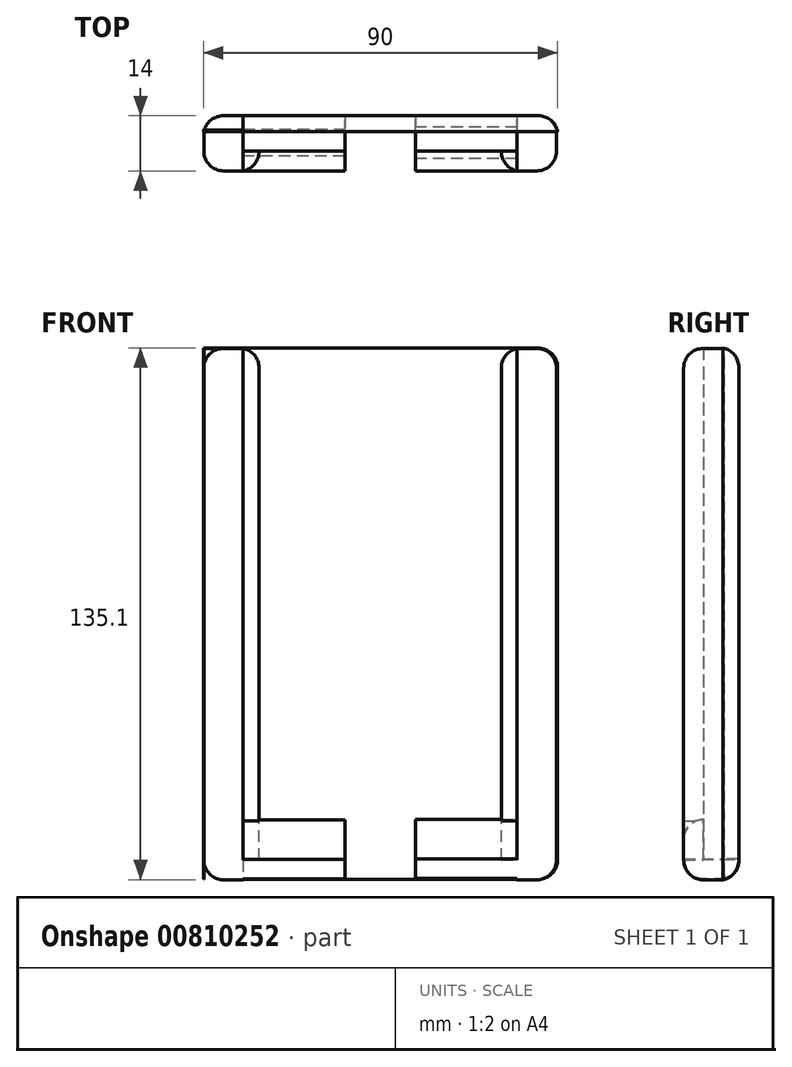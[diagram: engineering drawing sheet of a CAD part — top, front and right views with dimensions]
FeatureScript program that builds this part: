
annotation { "Feature Type Name" : "Feature", "Feature Type Description" : "" }
export const myFeature = defineFeature(function(context is Context, id is Id, definition is map)
    precondition{}
    {
        {
            var Q0;
            Q0=qCreatedBy(makeId("Front.planeOp"),FACE);
            var sketch = newSketch(context, id + "F0", { "sketchPlane" : qUnion([Q0])});
            skLineSegment(sketch, "E0.bottom", {"start": v(45, -67.5) * mm, "end": v(-45, -67.5) * mm});
            skLineSegment(sketch, "E0.top", {"start": v(45, 67.5) * mm, "end": v(-45, 67.5) * mm});
            skLineSegment(sketch, "E0.left", {"start": v(45, -67.5) * mm, "end": v(45, 67.5) * mm});
            skLineSegment(sketch, "E0.right", {"start": v(-45, -67.5) * mm, "end": v(-45, 67.5) * mm});
            skPoint(sketch, "E0.middle", {"position": v(0, 0) * mm});
            skSolve(sketch);
        }
        {
            var Q0;
            Q0=makeQuery(id+"F0.imprint","IMPRINT",FACE,{"disambiguationData":[TD([[makeQuery(id+"F0.imprint","IMPRINT",EDGE,{"derivedFrom":sQuery(id+"F0.wireOp",EDGE,"E0.bottom")}),-1.0]])]});
            var sketch = newSketch(context, id + "F1", { "sketchPlane" : qUnion([Q0])});
            skLineSegment(sketch, "E1.bottom", {"start": v(-44.9, -67.6) * mm, "end": v(-34.9, -67.6) * mm});
            skLineSegment(sketch, "E1.top", {"start": v(-44.9, 67.4) * mm, "end": v(-34.9, 67.4) * mm});
            skLineSegment(sketch, "E1.left", {"start": v(-44.9, -67.6) * mm, "end": v(-44.9, 67.4) * mm});
            skLineSegment(sketch, "E1.right", {"start": v(-34.9, -67.6) * mm, "end": v(-34.9, 67.4) * mm});
            skSolve(sketch);
        }
        {
            var Q0;
            Q0=makeQuery(id+"F0.imprint","IMPRINT",FACE,{"disambiguationData":[TD([[makeQuery(id+"F0.imprint","IMPRINT",EDGE,{"derivedFrom":sQuery(id+"F0.wireOp",EDGE,"E0.bottom")}),-1.0]])]});
            var sketch = newSketch(context, id + "F2", { "sketchPlane" : qUnion([Q0])});
            skLineSegment(sketch, "E2.bottom", {"start": v(44.68, -67.6) * mm, "end": v(34.68, -67.6) * mm});
            skLineSegment(sketch, "E2.top", {"start": v(44.68, 67.4) * mm, "end": v(34.68, 67.4) * mm});
            skLineSegment(sketch, "E2.left", {"start": v(44.68, -67.6) * mm, "end": v(44.68, 67.4) * mm});
            skLineSegment(sketch, "E2.right", {"start": v(34.68, -67.6) * mm, "end": v(34.68, 67.4) * mm});
            skSolve(sketch);
        }
        {
            var Q0;
            Q0=qCreatedBy(makeId("Front.planeOp"),FACE);
            var sketch = newSketch(context, id + "F3", { "sketchPlane" : qUnion([Q0])});
            skLineSegment(sketch, "E3.bottom", {"start": v(34.83, -67.26) * mm, "end": v(8.83, -67.26) * mm});
            skLineSegment(sketch, "E3.top", {"start": v(34.83, -62.26) * mm, "end": v(8.83, -62.26) * mm});
            skLineSegment(sketch, "E3.left", {"start": v(34.83, -67.26) * mm, "end": v(34.83, -62.26) * mm});
            skLineSegment(sketch, "E3.right", {"start": v(8.83, -67.26) * mm, "end": v(8.83, -62.26) * mm});
            skSolve(sketch);
        }
        {
            var Q0;
            Q0=qCreatedBy(makeId("Front.planeOp"),FACE);
            var sketch = newSketch(context, id + "F4", { "sketchPlane" : qUnion([Q0])});
            skLineSegment(sketch, "E4.bottom", {"start": v(-35.09, -67.43) * mm, "end": v(-9.09, -67.43) * mm});
            skLineSegment(sketch, "E4.top", {"start": v(-35.09, -62.43) * mm, "end": v(-9.09, -62.43) * mm});
            skLineSegment(sketch, "E4.left", {"start": v(-35.09, -67.43) * mm, "end": v(-35.09, -62.43) * mm});
            skLineSegment(sketch, "E4.right", {"start": v(-9.09, -67.43) * mm, "end": v(-9.09, -62.43) * mm});
            skSolve(sketch);
        }
        {
            var Q0;
            Q0=qSketchRegion(id+"F1",true);
            extrude(context, id + "F5", {"entities" : qUnion([Q0]), "depth" : 4 * mm, "offsetDistance" : 25 * mm});
        }
        {
            var Q0;
            Q0=qSketchRegion(id+"F2",true);
            extrude(context, id + "F6", {"entities" : qUnion([Q0]), "depth" : 4 * mm, "offsetDistance" : 25 * mm});
        }
        {
            var Q0;
            Q0=qSketchRegion(id+"F3",true);
            extrude(context, id + "F7", {"entities" : qUnion([Q0]), "operationType" : NewBodyOperationType.ADD, "depth" : 4 * mm, "offsetDistance" : 25 * mm});
        }
        {
            var Q0;
            Q0=qSketchRegion(id+"F4",true);
            extrude(context, id + "F8", {"entities" : qUnion([Q0]), "operationType" : NewBodyOperationType.ADD, "depth" : 4 * mm, "offsetDistance" : 25 * mm});
        }
        {
            var Q0;
            {var subQ1=sQuery(id+"F1.wireOp",EDGE,"E1.top");Q0=makeQuery(id+"F1.imprint","IMPRINT",FACE,{"disambiguationData":[TD([[makeQuery(id+"F1.imprint","IMPRINT",EDGE,{"derivedFrom":subQ1}),1.0]])]});}
            extrude(context, id + "F9", {"entities" : qUnion([Q0]), "depth" : 4 * mm, "offsetDistance" : 25 * mm});
        }
        {
            var Q0;
            Q0=makeQuery(id+"F8.boolean.opBoolean","MERGE",FACE,{"derivedFrom":[makeQuery(id+"F5.opExtrude","CAP_FACE",FACE,{"disambiguationData":[OSD([sQuery(id+"F1.wireOp",EDGE,"E1.bottom"),sQuery(id+"F1.wireOp",EDGE,"E1.top"),sQuery(id+"F1.wireOp",EDGE,"E1.left"),sQuery(id+"F1.wireOp",EDGE,"E1.right")])],"isStart":false}),makeQuery(id+"F8.opExtrude","CAP_FACE",FACE,{"disambiguationData":[OSD([sQuery(id+"F4.wireOp",EDGE,"E4.bottom"),sQuery(id+"F4.wireOp",EDGE,"E4.top"),sQuery(id+"F4.wireOp",EDGE,"E4.left"),sQuery(id+"F4.wireOp",EDGE,"E4.right")])],"isStart":false})]});
            var Q1;
            Q1=makeQuery(id+"F7.boolean.opBoolean","MERGE",FACE,{"derivedFrom":[makeQuery(id+"F6.opExtrude","CAP_FACE",FACE,{"disambiguationData":[OSD([sQuery(id+"F2.wireOp",EDGE,"E2.bottom"),sQuery(id+"F2.wireOp",EDGE,"E2.top"),sQuery(id+"F2.wireOp",EDGE,"E2.left"),sQuery(id+"F2.wireOp",EDGE,"E2.right")])],"isStart":false}),makeQuery(id+"F7.opExtrude","CAP_FACE",FACE,{"disambiguationData":[OSD([sQuery(id+"F3.wireOp",EDGE,"E3.bottom"),sQuery(id+"F3.wireOp",EDGE,"E3.top"),sQuery(id+"F3.wireOp",EDGE,"E3.left"),sQuery(id+"F3.wireOp",EDGE,"E3.right")])],"isStart":false})]});
            extrude(context, id + "F10", {"entities" : qUnion([Q0, Q1]), "depth" : 10 * mm, "offsetDistance" : 25 * mm});
        }
        {
            var Q0;
            Q0=makeQuery(id+"F10.opExtrude","SWEPT_FACE",FACE,{"disambiguationData":[OSD([sQuery(id+"F3.wireOp",EDGE,"E3.top")])]});
            var sketch = newSketch(context, id + "F11", { "sketchPlane" : qUnion([Q0])});
            skLineSegment(sketch, "E5.bottom", {"start": v(8.83, -14) * mm, "end": v(34.68, -14) * mm});
            skLineSegment(sketch, "E5.top", {"start": v(8.83, -9) * mm, "end": v(34.68, -9) * mm});
            skLineSegment(sketch, "E5.left", {"start": v(8.83, -14) * mm, "end": v(8.83, -9) * mm});
            skLineSegment(sketch, "E5.right", {"start": v(34.68, -14) * mm, "end": v(34.68, -9) * mm});
            skSolve(sketch);
        }
        {
            var Q0;
            Q0=makeQuery(id+"F10.opExtrude","SWEPT_FACE",FACE,{"disambiguationData":[OSD([sQuery(id+"F4.wireOp",EDGE,"E4.top")])]});
            var sketch = newSketch(context, id + "F12", { "sketchPlane" : qUnion([Q0])});
            skLineSegment(sketch, "E6.bottom", {"start": v(-34.9, -14) * mm, "end": v(-9.09, -14) * mm});
            skLineSegment(sketch, "E6.top", {"start": v(-34.9, -9) * mm, "end": v(-9.09, -9) * mm});
            skLineSegment(sketch, "E6.left", {"start": v(-34.9, -14) * mm, "end": v(-34.9, -9) * mm});
            skLineSegment(sketch, "E6.right", {"start": v(-9.09, -14) * mm, "end": v(-9.09, -9) * mm});
            skSolve(sketch);
        }
        {
            var Q0;
            Q0=makeQuery(id+"F12.imprint","IMPRINT",FACE,{"disambiguationData":[TD([[makeQuery(id+"F12.imprint","IMPRINT",EDGE,{"derivedFrom":sQuery(id+"F12.wireOp",EDGE,"E6.bottom")}),1.0]])]});
            var Q1;
            Q1=makeQuery(id+"F11.imprint","IMPRINT",FACE,{"disambiguationData":[TD([[makeQuery(id+"F11.imprint","IMPRINT",EDGE,{"derivedFrom":sQuery(id+"F11.wireOp",EDGE,"E5.bottom")}),-1.0]])]});
            extrude(context, id + "F13", {"entities" : qUnion([Q0, Q1]), "depth" : 10 * mm, "offsetDistance" : 25 * mm});
        }
        {
            var Q0;
            {var subQ0=sQuery(id+"F2.wireOp",EDGE,"E2.right");var subQ2=sQuery(id+"F2.wireOp",EDGE,"E2.top");Q0=makeQuery(id+"F10.opExtrude","SWEPT_FACE",FACE,{"disambiguationData":[OSD([subQ0]),TDD([makeQuery(id+"F7.boolean.opBoolean","SPLIT",EDGE,{"disambiguationData":[TD([makeQuery(id+"F6.opExtrude","SWEPT_FACE",FACE,{"disambiguationData":[OSD([subQ2])]})])],"derivedFrom":makeQuery(id+"F6.opExtrude","CAP_EDGE",EDGE,{"disambiguationData":[OSD([subQ0])],"isStart":false})})])]});}
            var sketch = newSketch(context, id + "F14", { "sketchPlane" : qUnion([Q0])});
            skLineSegment(sketch, "E7.bottom", {"start": v(14, 67.4) * mm, "end": v(9, 67.4) * mm});
            skLineSegment(sketch, "E7.top", {"start": v(14, -52.6) * mm, "end": v(9, -52.6) * mm});
            skLineSegment(sketch, "E7.left", {"start": v(14, 67.4) * mm, "end": v(14, -52.6) * mm});
            skLineSegment(sketch, "E7.right", {"start": v(9, 67.4) * mm, "end": v(9, -52.6) * mm});
            skSolve(sketch);
        }
        {
            var Q0;
            Q0=makeQuery(id+"F14.imprint","IMPRINT",FACE,{"disambiguationData":[TD([[makeQuery(id+"F14.imprint","IMPRINT",EDGE,{"derivedFrom":sQuery(id+"F14.wireOp",EDGE,"E7.bottom")}),1.0]])]});
            extrude(context, id + "F15", {"entities" : qUnion([Q0]), "depth" : 4 * mm, "offsetDistance" : 25 * mm});
        }
        {
            var Q0;
            {var subQ1=sQuery(id+"F1.wireOp",EDGE,"E1.right");var subQ2=sQuery(id+"F1.wireOp",EDGE,"E1.top");Q0=makeQuery(id+"F10.opExtrude","SWEPT_FACE",FACE,{"disambiguationData":[OSD([subQ1]),TDD([makeQuery(id+"F8.boolean.opBoolean","SPLIT",EDGE,{"disambiguationData":[TD([makeQuery(id+"F5.opExtrude","SWEPT_FACE",FACE,{"disambiguationData":[OSD([subQ2])]})])],"derivedFrom":makeQuery(id+"F5.opExtrude","CAP_EDGE",EDGE,{"disambiguationData":[OSD([subQ1])],"isStart":false})})])]});}
            var sketch = newSketch(context, id + "F16", { "sketchPlane" : qUnion([Q0])});
            skLineSegment(sketch, "E8.bottom", {"start": v(-14, 67.4) * mm, "end": v(-9, 67.4) * mm});
            skLineSegment(sketch, "E8.top", {"start": v(-14, -52.6) * mm, "end": v(-9, -52.6) * mm});
            skLineSegment(sketch, "E8.left", {"start": v(-14, 67.4) * mm, "end": v(-14, -52.6) * mm});
            skLineSegment(sketch, "E8.right", {"start": v(-9, 67.4) * mm, "end": v(-9, -52.6) * mm});
            skSolve(sketch);
        }
        {
            var Q0;
            Q0=makeQuery(id+"F16.imprint","IMPRINT",FACE,{"disambiguationData":[TD([[makeQuery(id+"F16.imprint","IMPRINT",EDGE,{"derivedFrom":sQuery(id+"F16.wireOp",EDGE,"E8.bottom")}),-1.0]])]});
            extrude(context, id + "F17", {"entities" : qUnion([Q0]), "depth" : 4 * mm, "offsetDistance" : 25 * mm});
        }
        {
            var Q0;
            Q0=makeQuery(id+"F10.opExtrude","SWEPT_EDGE",EDGE,{"disambiguationData":[OSD([sQuery(id+"F1.wireOp",EDGE,"E1.bottom"),sQuery(id+"F1.wireOp",EDGE,"E1.left")])]});
            var Q1;
            Q1=makeQuery(id+"F9.opExtrude","SWEPT_EDGE",EDGE,{"disambiguationData":[OSD([sQuery(id+"F0.wireOp",EDGE,"E0.bottom"),sQuery(id+"F0.wireOp",EDGE,"E0.right")])]});
            fillet(context, id + "F18", {"entities" : qUnion([Q0, Q1]), "radius" : 5 * mm, "tangentPropagation" : true, "allowEdgeOverflow" : false});
        }
        {
            var Q0;
            Q0=makeQuery(id+"F5.opExtrude","SWEPT_EDGE",EDGE,{"disambiguationData":[OSD([sQuery(id+"F1.wireOp",EDGE,"E1.bottom"),sQuery(id+"F1.wireOp",EDGE,"E1.left")])]});
            var Q1;
            {var subQ0=sQuery(id+"F0.wireOp",EDGE,"E0.right");Q1=makeQuery(id+"F18.opFillet","BLEND_EDGE",EDGE,{"blendedFrom":[makeQuery(id+"F9.opExtrude","SWEPT_EDGE",EDGE,{"disambiguationData":[OSD([sQuery(id+"F0.wireOp",EDGE,"E0.bottom"),subQ0])]}),makeQuery(id+"F9.opExtrude","SWEPT_FACE",FACE,{"disambiguationData":[OSD([subQ0])]})],"blendedInto":[makeQuery(id+"F9.opExtrude","SWEPT_FACE",FACE,{"disambiguationData":[OSD([subQ0])]})]});}
            fillet(context, id + "F19", {"entities" : qUnion([Q0, Q1]), "radius" : 5 * mm, "tangentPropagation" : true, "allowEdgeOverflow" : false});
        }
        {
            var Q0;
            Q0=makeQuery(id+"F9.opExtrude","SWEPT_EDGE",EDGE,{"disambiguationData":[OSD([sQuery(id+"F0.wireOp",EDGE,"E0.bottom"),sQuery(id+"F0.wireOp",EDGE,"E0.left")])]});
            var Q1;
            Q1=makeQuery(id+"F10.opExtrude","SWEPT_EDGE",EDGE,{"disambiguationData":[OSD([sQuery(id+"F2.wireOp",EDGE,"E2.bottom"),sQuery(id+"F2.wireOp",EDGE,"E2.left")])]});
            fillet(context, id + "F20", {"entities" : qUnion([Q0, Q1]), "radius" : 5 * mm, "tangentPropagation" : true, "allowEdgeOverflow" : false});
        }
        {
            var Q0;
            Q0=makeQuery(id+"F6.opExtrude","SWEPT_EDGE",EDGE,{"disambiguationData":[OSD([sQuery(id+"F2.wireOp",EDGE,"E2.bottom"),sQuery(id+"F2.wireOp",EDGE,"E2.left")])]});
            fillet(context, id + "F21", {"entities" : qUnion([Q0]), "radius" : 5 * mm, "tangentPropagation" : true, "allowEdgeOverflow" : false});
        }
        {
            var Q0;
            Q0=makeQuery(id+"F10.opExtrude","SWEPT_EDGE",EDGE,{"disambiguationData":[OSD([sQuery(id+"F1.wireOp",EDGE,"E1.top"),sQuery(id+"F1.wireOp",EDGE,"E1.left")])]});
            fillet(context, id + "F22", {"entities" : qUnion([Q0]), "radius" : 5 * mm, "tangentPropagation" : true, "allowEdgeOverflow" : false});
        }
        {
            var Q0;
            Q0=makeQuery(id+"F10.opExtrude","SWEPT_EDGE",EDGE,{"disambiguationData":[OSD([sQuery(id+"F2.wireOp",EDGE,"E2.top"),sQuery(id+"F2.wireOp",EDGE,"E2.left")])]});
            var Q1;
            Q1=makeQuery(id+"F9.opExtrude","SWEPT_EDGE",EDGE,{"disambiguationData":[OSD([sQuery(id+"F0.wireOp",EDGE,"E0.top"),sQuery(id+"F0.wireOp",EDGE,"E0.left")])]});
            fillet(context, id + "F23", {"entities" : qUnion([Q0, Q1]), "radius" : 5 * mm, "tangentPropagation" : true, "allowEdgeOverflow" : false});
        }
        {
            var Q0;
            Q0=makeQuery(id+"F10.opExtrude","CAP_EDGE",EDGE,{"disambiguationData":[OSD([sQuery(id+"F1.wireOp",EDGE,"E1.left")])],"isStart":false});
            fillet(context, id + "F24", {"entities" : qUnion([Q0]), "radius" : 5 * mm, "tangentPropagation" : true, "allowEdgeOverflow" : false});
        }
        {
            var Q0;
            Q0=makeQuery(id+"F17.opExtrude","SWEPT_EDGE",EDGE,{"disambiguationData":[OSD([sQuery(id+"F16.wireOp",EDGE,"E8.bottom"),sQuery(id+"F16.wireOp",EDGE,"E8.left")])]});
            fillet(context, id + "F25", {"entities" : qUnion([Q0]), "radius" : 5 * mm, "tangentPropagation" : true, "allowEdgeOverflow" : false});
        }
        {
            var Q0;
            Q0=makeQuery(id+"F10.opExtrude","CAP_EDGE",EDGE,{"disambiguationData":[OSD([sQuery(id+"F2.wireOp",EDGE,"E2.left")])],"isStart":false});
            fillet(context, id + "F26", {"entities" : qUnion([Q0]), "radius" : 5 * mm, "tangentPropagation" : true, "allowEdgeOverflow" : false});
        }
        {
            var Q0;
            Q0=makeQuery(id+"F15.opExtrude","SWEPT_EDGE",EDGE,{"disambiguationData":[OSD([sQuery(id+"F14.wireOp",EDGE,"E7.bottom"),sQuery(id+"F14.wireOp",EDGE,"E7.left")])]});
            fillet(context, id + "F27", {"entities" : qUnion([Q0]), "radius" : 5 * mm, "tangentPropagation" : true, "allowEdgeOverflow" : false});
        }
        {
            var Q0;
            Q0=makeQuery(id+"F15.opExtrude","CAP_EDGE",EDGE,{"disambiguationData":[OSD([sQuery(id+"F14.wireOp",EDGE,"E7.left")])],"isStart":false});
            fillet(context, id + "F28", {"entities" : qUnion([Q0]), "radius" : 5 * mm, "tangentPropagation" : true, "allowEdgeOverflow" : false});
        }
        {
            var Q0;
            Q0=makeQuery(id+"F17.opExtrude","CAP_EDGE",EDGE,{"disambiguationData":[OSD([sQuery(id+"F16.wireOp",EDGE,"E8.left")])],"isStart":false});
            fillet(context, id + "F29", {"entities" : qUnion([Q0]), "radius" : 5 * mm, "tangentPropagation" : true, "allowEdgeOverflow" : false});
        }
        {
            var Q0;
            Q0=makeQuery(id+"F13.opExtrude","CAP_EDGE",EDGE,{"disambiguationData":[OSD([sQuery(id+"F12.wireOp",EDGE,"E6.bottom")])],"isStart":false});
            fillet(context, id + "F30", {"entities" : qUnion([Q0]), "radius" : 5 * mm, "tangentPropagation" : true, "allowEdgeOverflow" : false});
        }
        {
            var Q0;
            Q0=makeQuery(id+"F13.opExtrude","CAP_EDGE",EDGE,{"disambiguationData":[OSD([sQuery(id+"F11.wireOp",EDGE,"E5.bottom")])],"isStart":false});
            fillet(context, id + "F31", {"entities" : qUnion([Q0]), "radius" : 5 * mm, "tangentPropagation" : true, "allowEdgeOverflow" : false});
        }
        {
            var Q0;
            Q0=makeQuery(id+"F6.opExtrude","SWEPT_EDGE",EDGE,{"disambiguationData":[OSD([sQuery(id+"F2.wireOp",EDGE,"E2.top"),sQuery(id+"F2.wireOp",EDGE,"E2.left")])]});
            fillet(context, id + "F32", {"entities" : qUnion([Q0]), "radius" : 5 * mm, "tangentPropagation" : true, "allowEdgeOverflow" : false});
        }
        {
            var Q0;
            Q0=makeQuery(id+"F9.opExtrude","CAP_EDGE",EDGE,{"disambiguationData":[OSD([sQuery(id+"F0.wireOp",EDGE,"E0.right")])],"isStart":true});
            fillet(context, id + "F33", {"entities" : qUnion([Q0]), "radius" : 5 * mm, "tangentPropagation" : true, "allowEdgeOverflow" : false});
        }
        {
            var Q0;
            Q0=makeQuery(id+"F5.opExtrude","CAP_EDGE",EDGE,{"disambiguationData":[OSD([sQuery(id+"F1.wireOp",EDGE,"E1.left")])],"isStart":true});
            fillet(context, id + "F34", {"entities" : qUnion([Q0]), "radius" : 5 * mm, "tangentPropagation" : true, "allowEdgeOverflow" : false});
        }
        {
            var Q0;
            Q0=makeQuery(id+"F9.opExtrude","CAP_EDGE",EDGE,{"disambiguationData":[OSD([sQuery(id+"F0.wireOp",EDGE,"E0.left")])],"isStart":true});
            fillet(context, id + "F35", {"entities" : qUnion([Q0]), "radius" : 5 * mm, "tangentPropagation" : true, "allowEdgeOverflow" : false});
        }
        {
            var Q0;
            Q0=makeQuery(id+"F6.opExtrude","CAP_EDGE",EDGE,{"disambiguationData":[OSD([sQuery(id+"F2.wireOp",EDGE,"E2.left")])],"isStart":true});
            fillet(context, id + "F36", {"entities" : qUnion([Q0]), "radius" : 5 * mm, "tangentPropagation" : true, "allowEdgeOverflow" : false});
        }
        {
            var Q0;
            Q0=makeQuery(id+"F5.opExtrude","CAP_EDGE",EDGE,{"disambiguationData":[OSD([sQuery(id+"F1.wireOp",EDGE,"E1.top")])],"isStart":true});
            fillet(context, id + "F37", {"entities" : qUnion([Q0]), "radius" : 5 * mm, "tangentPropagation" : true, "allowEdgeOverflow" : false});
        }
        {
            var Q0;
            Q0=makeQuery(id+"F17.opExtrude","SWEPT_FACE",FACE,{"disambiguationData":[OSD([sQuery(id+"F16.wireOp",EDGE,"E8.top")])]});
            extrude(context, id + "F38", {"entities" : qUnion([Q0]), "depth" : 10 * mm, "offsetDistance" : 25 * mm});
        }
        {
            var Q0;
            Q0=makeQuery(id+"F15.opExtrude","SWEPT_FACE",FACE,{"disambiguationData":[OSD([sQuery(id+"F14.wireOp",EDGE,"E7.top")])]});
            extrude(context, id + "F39", {"entities" : qUnion([Q0]), "depth" : 10 * mm, "offsetDistance" : 25 * mm});
        }
        {
            var Q0;
            Q0=makeQuery(id+"F37.opFillet","BLEND_EDGE",EDGE,{"blendedFrom":[makeQuery(id+"F5.opExtrude","CAP_EDGE",EDGE,{"disambiguationData":[OSD([sQuery(id+"F1.wireOp",EDGE,"E1.top")])],"isStart":true}),makeQuery(id+"F34.opFillet","BLEND_FACE",FACE,{"disambiguationData":[OSD([sQuery(id+"F1.wireOp",EDGE,"E1.left")])]})],"blendedInto":[makeQuery(id+"F34.opFillet","BLEND_FACE",FACE,{"disambiguationData":[OSD([sQuery(id+"F1.wireOp",EDGE,"E1.left")])]})]});
            fillet(context, id + "F40", {"entities" : qUnion([Q0]), "radius" : 5 * mm, "tangentPropagation" : true, "allowEdgeOverflow" : false});
        }
    });
